# Revit family: MH-Overflow_Updated
name_source: partatom
category: Plumbing Fixtures
units: mm (PartAtom-declared; Revit-internal decimal feet)

## family parameters
Always vertical = Yes
Cut with Voids When Loaded = No
OmniClass Number = 23.70.50.21.24.11
OmniClass Title = Roof Waste Water Drains
Part Type = Normal
Room Calculation Point = No
Round Connector Dimension = Use Diameter
Shared = No
Work Plane-Based = No

## types (4) — shared parameters
Default Elevation = 0"
Manufacturer = MIFAB

MIFAB
MIFAB
R1 = 3/16"
SC1 = 3/16"
SC2 = 1/8"
URL = www.mifab.com
id3 = 1/8"
r2 = 3/4"

## per-type parameters (varying)
| type | A | A' | B | B' | B01 | C | C' | C'1 | D | Description | Model | PIPE SIZE | PIPE SIZE' | RP1 | RP2 | id1 | linearL | linearW | max dia | od1 | od2 | od3 |
| MH-300_3"Ø | 19 3/8" | 9 11/16" | 17 13/16" | 8 15/16" | 8 1/2" | 10 11/16" | 5 5/16" | 5 3/4" | 3 9/16" | 3" HydroMax Siphonic Overflow Roof Drain | MH-300 | 3" | 1 1/2" | 3/16" | 3/16" | 3/16" | 1 5/8" | 3 9/16" | 9/16" | 3/8" | 5/16" | 3/16" |
| MH-400_4"Ø | 19 3/8" | 9 11/16" | 17 13/16" | 8 15/16" | 8 7/16" | 12 3/16" | 6 1/8" | 6 1/2" | 4 5/16" | 4" HydroMax Siphonic Overflow Roof Drain | MH-400 | 4" | 2" | 3/16" | 1/4" | 1/4" | 1 13/16" | 3 15/16" | 9/16" | 1/2" | 3/8" | 3/16" |
| MH-600_6"Ø | 25 3/16" | 12 5/8" | 22 5/16" | 11 1/8" | 10 9/16" | 15 9/16" | 7 3/4" | 8 3/16" | 4 3/4" | 6" HydroMax Siphonic Overflow Roof Drain | MH-600 | 6" | 3" | 1/4" | 1/4" | 1/4" | 2 9/16" | 5 1/2" | 1 1/4" | 9/16" | 1/2" | 1/4" |
| MH-500_5"Ø | 19 3/8" | 9 11/16" | 17 13/16" | 8 15/16" | 8 7/16" | 12 3/16" | 6 1/8" | 6 1/2" | 4 5/16" | 5" HydroMax Siphonic Overflow Roof Drain | MH-500 | 5" | 2 1/2" | 3/16" | 1/4" | 1/4" | 1 13/16" | 3 15/16" | 9/16" | 1/2" | 3/8" | 3/16" |

## geometry (parser evidence)
native form markers: Sweep x2
no freeform markers — native parametric forms only
